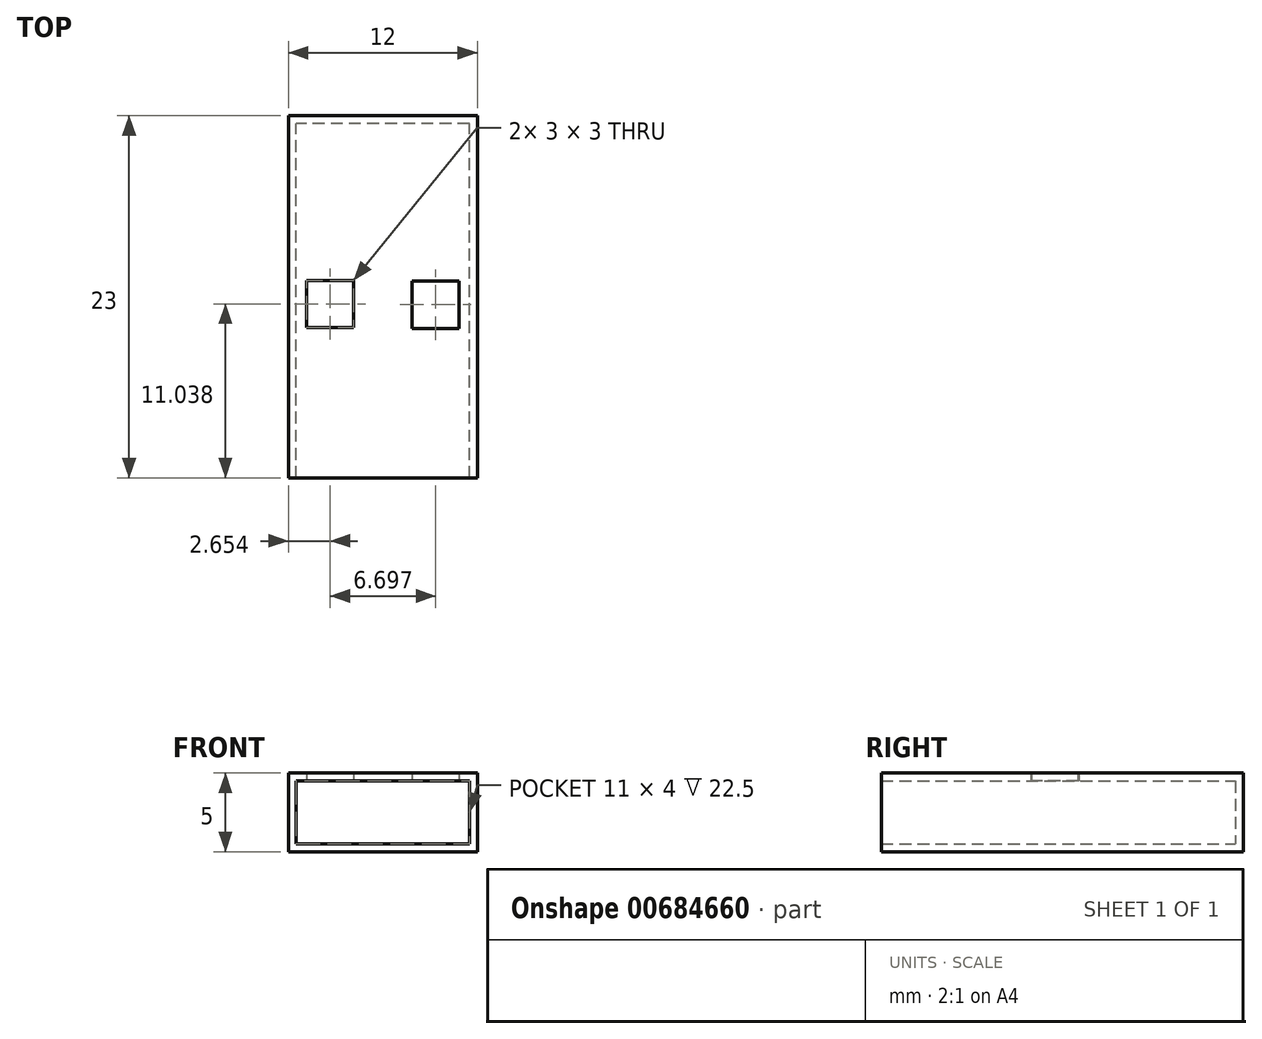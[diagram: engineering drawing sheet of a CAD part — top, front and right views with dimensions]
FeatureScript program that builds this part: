
annotation { "Feature Type Name" : "Feature", "Feature Type Description" : "" }
export const myFeature = defineFeature(function(context is Context, id is Id, definition is map)
    precondition{}
    {
        {
            var Q0;
            Q0=qCreatedBy(makeId("Front.planeOp"),FACE);
            var sketch = newSketch(context, id + "F0", { "sketchPlane" : qUnion([Q0])});
            skLineSegment(sketch, "E0.bottom", {"start": v(6, 2.5) * mm, "end": v(-6, 2.5) * mm});
            skLineSegment(sketch, "E0.top", {"start": v(6, -2.5) * mm, "end": v(-6, -2.5) * mm});
            skLineSegment(sketch, "E0.left", {"start": v(6, 2.5) * mm, "end": v(6, -2.5) * mm});
            skLineSegment(sketch, "E0.right", {"start": v(-6, 2.5) * mm, "end": v(-6, -2.5) * mm});
            skPoint(sketch, "E0.middle", {"position": v(0, 0) * mm});
            skSolve(sketch);
        }
        {
            var Q0;
            Q0=makeQuery(id+"F0.imprint","IMPRINT",FACE,{"disambiguationData":[TD([[makeQuery(id+"F0.imprint","IMPRINT",EDGE,{"derivedFrom":sQuery(id+"F0.wireOp",EDGE,"E0.bottom")}),1.0]])]});
            extrude(context, id + "F1", {"entities" : qUnion([Q0]), "depth" : 23 * mm, "offsetDistance" : 25 * mm});
        }
        {
            var Q0;
            Q0=makeQuery(id+"F1.opExtrude","CAP_FACE",FACE,{"disambiguationData":[OSD([sQuery(id+"F0.wireOp",EDGE,"E0.bottom"),sQuery(id+"F0.wireOp",EDGE,"E0.top"),sQuery(id+"F0.wireOp",EDGE,"E0.left"),sQuery(id+"F0.wireOp",EDGE,"E0.right")])],"isStart":false});
            shell(context, id + "F2", {"entities" : qUnion([Q0]), "thickness" : 0.5 * mm});
        }
        {
            var Q0;
            Q0=qCreatedBy(makeId("Top.planeOp"),FACE);
            var sketch = newSketch(context, id + "F3", { "sketchPlane" : qUnion([Q0])});
            skLineSegment(sketch, "E1.bottom", {"start": v(-4.85, -10.46) * mm, "end": v(-1.85, -10.46) * mm});
            skLineSegment(sketch, "E1.top", {"start": v(-4.85, -13.46) * mm, "end": v(-1.85, -13.46) * mm});
            skLineSegment(sketch, "E1.left", {"start": v(-4.85, -10.46) * mm, "end": v(-4.85, -13.46) * mm});
            skLineSegment(sketch, "E1.right", {"start": v(-1.85, -10.46) * mm, "end": v(-1.85, -13.46) * mm});
            skSolve(sketch);
        }
        {
            var Q0;
            Q0 = qSketchRegion(id + "F3", true);
            extrude(context, id + "F4", {"entities" : qUnion([Q0]), "operationType" : NewBodyOperationType.REMOVE, "depth" : 4.2 * mm, "offsetDistance" : 25 * mm});
        }
        {
            var Q0;
            Q0=qCreatedBy(makeId("Top.planeOp"),FACE);
            var sketch = newSketch(context, id + "F5", { "sketchPlane" : qUnion([Q0])});
            skLineSegment(sketch, "E2.bottom", {"start": v(1.85, -10.5) * mm, "end": v(4.85, -10.5) * mm});
            skLineSegment(sketch, "E2.top", {"start": v(1.85, -13.5) * mm, "end": v(4.85, -13.5) * mm});
            skLineSegment(sketch, "E2.left", {"start": v(1.85, -10.5) * mm, "end": v(1.85, -13.5) * mm});
            skLineSegment(sketch, "E2.right", {"start": v(4.85, -10.5) * mm, "end": v(4.85, -13.5) * mm});
            skSolve(sketch);
        }
        {
            var Q0;
            Q0 = qSketchRegion(id + "F5", true);
            extrude(context, id + "F6", {"entities" : qUnion([Q0]), "operationType" : NewBodyOperationType.REMOVE, "depth" : 6.2 * mm, "offsetDistance" : 25 * mm});
        }
    });
